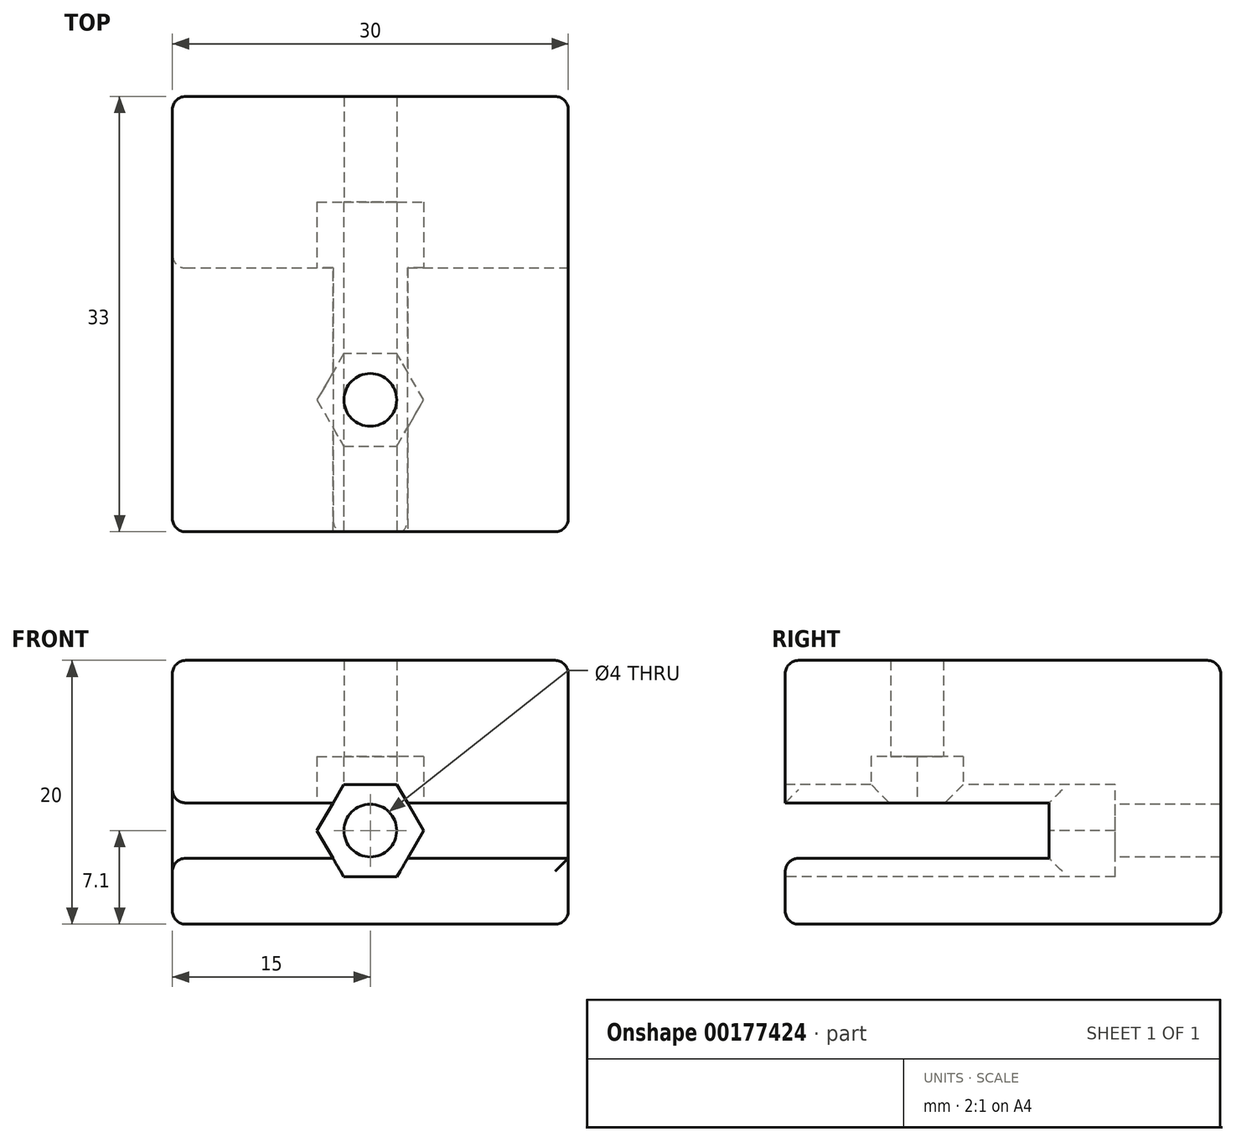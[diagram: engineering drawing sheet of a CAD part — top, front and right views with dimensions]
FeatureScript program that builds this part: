
annotation { "Feature Type Name" : "Feature", "Feature Type Description" : "" }
export const myFeature = defineFeature(function(context is Context, id is Id, definition is map)
    precondition{}
    {
        {
            var Q0;
            Q0=qCreatedBy(makeId("Top.planeOp"),FACE);
            var sketch = newSketch(context, id + "F0", { "sketchPlane" : qUnion([Q0])});
            skLineSegment(sketch, "E0.bottom", {"start": v(-15, 16.5) * mm, "end": v(15, 16.5) * mm});
            skLineSegment(sketch, "E0.top", {"start": v(-15, -16.5) * mm, "end": v(15, -16.5) * mm});
            skLineSegment(sketch, "E0.left", {"start": v(-15, 16.5) * mm, "end": v(-15, -16.5) * mm});
            skLineSegment(sketch, "E0.right", {"start": v(15, 16.5) * mm, "end": v(15, -16.5) * mm});
            skSolve(sketch);
        }
        {
            var Q0;
            Q0=makeQuery(id+"F0.imprint","IMPRINT",FACE,{"disambiguationData":[TD([[makeQuery(id+"F0.imprint","IMPRINT",EDGE,{"derivedFrom":sQuery(id+"F0.wireOp",EDGE,"E0.bottom")}),-1.0]])]});
            extrude(context, id + "F1", {"entities" : qUnion([Q0]), "depth" : 20 * mm});
        }
        {
            var Q0;
            Q0=makeQuery(id+"F1.opExtrude","SWEPT_FACE",FACE,{"disambiguationData":[OSD([sQuery(id+"F0.wireOp",EDGE,"E0.right")])]});
            var sketch = newSketch(context, id + "F2", { "sketchPlane" : qUnion([Q0])});
            skLineSegment(sketch, "E1", {"start": v(-16.5, 5) * mm, "end": v(3.5, 5) * mm});
            skLineSegment(sketch, "E2", {"start": v(3.5, 5) * mm, "end": v(3.5, 9.2) * mm});
            skLineSegment(sketch, "E3", {"start": v(3.5, 9.2) * mm, "end": v(-16.5, 9.2) * mm});
            skSolve(sketch);
        }
        {
            var Q0;
            {var subQ0=sQuery(id+"F2.wireOp",EDGE,"E1");Q0=makeQuery(id+"F2.imprint","IMPRINT",FACE,{"disambiguationData":[TD([[makeQuery(id+"F2.imprint","IMPRINT",EDGE,{"derivedFrom":subQ0}),1.0]])]});}
            extrude(context, id + "F3", {"entities" : qUnion([Q0]), "operationType" : NewBodyOperationType.REMOVE, "endBound" : BoundingType.THROUGH_ALL, "oppositeDirection" : true, "depth" : 25 * mm});
        }
        {
            var Q0;
            Q0=makeQuery(id+"F3.boolean.opBoolean","COPY",FACE,{"derivedFrom":makeQuery(id+"F3.opExtrude","SWEPT_FACE",FACE,{"disambiguationData":[OSD([sQuery(id+"F2.wireOp",EDGE,"E2")])]})});
            var sketch = newSketch(context, id + "F4", { "sketchPlane" : qUnion([Q0])});
            skPoint(sketch, "E4", {"position": v(0, 7.1) * mm});
            skCircle(sketch, "E5.cCircle", {"center": v(0, 7.1) * mm, "radius": 3.5 * mm, "construction": true});
            skLineSegment(sketch, "E5.0", {"start": v(2.02, 3.6) * mm, "end": v(-2.02, 3.6) * mm});
            skLineSegment(sketch, "E5.1", {"start": v(-2.02, 3.6) * mm, "end": v(-4.04, 7.1) * mm});
            skLineSegment(sketch, "E5.2", {"start": v(-4.04, 7.1) * mm, "end": v(-2.02, 10.6) * mm});
            skLineSegment(sketch, "E5.3", {"start": v(-2.02, 10.6) * mm, "end": v(2.02, 10.6) * mm});
            skLineSegment(sketch, "E5.4", {"start": v(2.02, 10.6) * mm, "end": v(4.04, 7.1) * mm});
            skLineSegment(sketch, "E5.5", {"start": v(4.04, 7.1) * mm, "end": v(2.02, 3.6) * mm});
            skPoint(sketch, "E5.0.midPoint", {"position": v(0, 3.6) * mm});
            skCircle(sketch, "E6", {"center": v(0, 7.1) * mm, "radius": 2 * mm});
            skSolve(sketch);
        }
        {
            var Q0;
            {var subQ0=sQuery(id+"F4.wireOp",EDGE,"E5.3");Q0=makeQuery(id+"F4.imprint","IMPRINT",FACE,{"disambiguationData":[TD([[makeQuery(id+"F4.imprint","IMPRINT",EDGE,{"derivedFrom":subQ0}),-1.0]])]});}
            var Q1;
            {var subQ8=sQuery(id+"F4.wireOp",EDGE,"E5.2");var subQ9=sQuery(id+"F4.wireOp",EDGE,"E5.1");var subQ10=makeQuery(id+"F4.imprint","INTERSECT",VERTEX,{"derivedFrom":[subQ9,subQ8]});Q1=makeQuery(id+"F4.imprint","IMPRINT",FACE,{"disambiguationData":[TD([[makeQuery(id+"F4.imprint","IMPRINT",EDGE,{"disambiguationData":[TD([[subQ10,1.0]])],"derivedFrom":subQ9}),-1.0]])]});}
            var Q2;
            {var subQ0=sQuery(id+"F4.wireOp",EDGE,"E5.0");Q2=makeQuery(id+"F4.imprint","IMPRINT",FACE,{"disambiguationData":[TD([[makeQuery(id+"F4.imprint","IMPRINT",EDGE,{"derivedFrom":subQ0}),-1.0]])]});}
            extrude(context, id + "F5", {"entities" : qUnion([Q0, Q1, Q2]), "operationType" : NewBodyOperationType.REMOVE, "oppositeDirection" : true, "depth" : 5 * mm, "hasSecondDirection" : true, "secondDirectionBound" : SecondDirectionBoundingType.THROUGH_ALL, "secondDirectionOppositeDirection" : false, "secondDirectionDepth" : 25 * mm});
        }
        {
            var Q0;
            Q0=makeQuery(id+"F5.boolean.opBoolean","SPLIT",FACE,{"disambiguationData":[TD([makeQuery(id+"F5.opExtrude","SWEPT_FACE",FACE,{"disambiguationData":[OSD([sQuery(id+"F4.wireOp",EDGE,"E6")])]})])],"derivedFrom":makeQuery(id+"F3.boolean.opBoolean","COPY",FACE,{"derivedFrom":makeQuery(id+"F3.opExtrude","SWEPT_FACE",FACE,{"disambiguationData":[OSD([sQuery(id+"F2.wireOp",EDGE,"E2")])]})})});
            extrude(context, id + "F6", {"entities" : qUnion([Q0]), "operationType" : NewBodyOperationType.REMOVE, "endBound" : BoundingType.THROUGH_ALL, "oppositeDirection" : true, "depth" : 25 * mm});
        }
        {
            var Q0;
            Q0=makeQuery(id+"F5.boolean.opBoolean","SPLIT",FACE,{"disambiguationData":[TD([makeQuery(id+"F1.opExtrude","SWEPT_FACE",FACE,{"disambiguationData":[OSD([sQuery(id+"F0.wireOp",EDGE,"E0.left")])]})])],"derivedFrom":makeQuery(id+"F3.boolean.opBoolean","COPY",FACE,{"derivedFrom":makeQuery(id+"F3.opExtrude","SWEPT_FACE",FACE,{"disambiguationData":[OSD([sQuery(id+"F2.wireOp",EDGE,"E3")])]})})});
            var sketch = newSketch(context, id + "F7", { "sketchPlane" : qUnion([Q0])});
            skPoint(sketch, "E7", {"position": v(0, 6.5) * mm});
            skLineSegment(sketch, "E8.0.0", {"start": v(-2.83, -3.5) * mm, "end": v(-2.83, 16.5) * mm});
            skLineSegment(sketch, "E8.0.1", {"start": v(-2.83, 16.5) * mm, "end": v(-15, 16.5) * mm});
            skLineSegment(sketch, "E8.0.2", {"start": v(-15, 16.5) * mm, "end": v(-15, -3.5) * mm});
            skLineSegment(sketch, "E8.0.3", {"start": v(-15, -3.5) * mm, "end": v(-2.83, -3.5) * mm});
            skLineSegment(sketch, "E9.0.0", {"start": v(2.83, 16.5) * mm, "end": v(2.83, -3.5) * mm});
            skLineSegment(sketch, "E9.0.1", {"start": v(2.83, -3.5) * mm, "end": v(15, -3.5) * mm});
            skLineSegment(sketch, "E9.0.2", {"start": v(15, -3.5) * mm, "end": v(15, 16.5) * mm});
            skLineSegment(sketch, "E9.0.3", {"start": v(15, 16.5) * mm, "end": v(2.83, 16.5) * mm});
            skCircle(sketch, "E10", {"center": v(0, 6.5) * mm, "radius": 2 * mm});
            skCircle(sketch, "E11.cCircle", {"center": v(0, 6.5) * mm, "radius": 3.5 * mm, "construction": true});
            skLineSegment(sketch, "E11.0", {"start": v(2.02, 3) * mm, "end": v(-2.02, 3) * mm});
            skLineSegment(sketch, "E11.1", {"start": v(-2.02, 3) * mm, "end": v(-4.04, 6.5) * mm});
            skLineSegment(sketch, "E11.2", {"start": v(-4.04, 6.5) * mm, "end": v(-2.02, 10) * mm});
            skLineSegment(sketch, "E11.3", {"start": v(-2.02, 10) * mm, "end": v(2.02, 10) * mm});
            skLineSegment(sketch, "E11.4", {"start": v(2.02, 10) * mm, "end": v(4.04, 6.5) * mm});
            skLineSegment(sketch, "E11.5", {"start": v(4.04, 6.5) * mm, "end": v(2.02, 3) * mm});
            skPoint(sketch, "E11.0.midPoint", {"position": v(0, 3) * mm});
            skSolve(sketch);
        }
        {
            var Q0;
            Q0=makeQuery(id+"F7.imprint","IMPRINT",FACE,{"disambiguationData":[TD([[makeQuery(id+"F7.imprint","IMPRINT",EDGE,{"derivedFrom":sQuery(id+"F7.wireOp",EDGE,"E10")}),1.0]])]});
            extrude(context, id + "F8", {"entities" : qUnion([Q0]), "operationType" : NewBodyOperationType.REMOVE, "endBound" : BoundingType.THROUGH_ALL, "oppositeDirection" : true, "depth" : 25 * mm});
        }
        {
            var Q0;
            Q0=makeQuery(id+"F7.imprint","IMPRINT",FACE,{"disambiguationData":[TD([[makeQuery(id+"F7.imprint","IMPRINT",EDGE,{"derivedFrom":sQuery(id+"F7.wireOp",EDGE,"E10")}),-1.0]])]});
            var Q1;
            {var subQ0=sQuery(id+"F7.wireOp",EDGE,"E11.2");var subQ1=sQuery(id+"F7.wireOp",EDGE,"E8.0.0");var subQ2=makeQuery(id+"F7.imprint","INTERSECT",VERTEX,{"derivedFrom":[subQ1,subQ0]});Q1=makeQuery(id+"F7.imprint","IMPRINT",FACE,{"disambiguationData":[TD([[makeQuery(id+"F7.imprint","IMPRINT",EDGE,{"disambiguationData":[TD([[subQ2,-1.0]])],"derivedFrom":subQ1}),-1.0]])]});}
            var Q2;
            {var subQ0=sQuery(id+"F7.wireOp",EDGE,"E11.4");var subQ1=sQuery(id+"F7.wireOp",EDGE,"E9.0.0");var subQ2=makeQuery(id+"F7.imprint","INTERSECT",VERTEX,{"derivedFrom":[subQ1,subQ0]});Q2=makeQuery(id+"F7.imprint","IMPRINT",FACE,{"disambiguationData":[TD([[makeQuery(id+"F7.imprint","IMPRINT",EDGE,{"disambiguationData":[TD([[subQ2,-1.0]])],"derivedFrom":subQ1}),1.0]])]});}
            extrude(context, id + "F9", {"entities" : qUnion([Q0, Q1, Q2]), "operationType" : NewBodyOperationType.REMOVE, "oppositeDirection" : true, "depth" : 3.5 * mm});
        }
        {
            var Q0;
            Q0=makeQuery(id+"F1.opExtrude","CAP_EDGE",EDGE,{"disambiguationData":[OSD([sQuery(id+"F0.wireOp",EDGE,"E0.bottom")])],"isStart":true});
            var Q1;
            Q1=makeQuery(id+"F1.opExtrude","SWEPT_EDGE",EDGE,{"disambiguationData":[OSD([sQuery(id+"F0.wireOp",EDGE,"E0.bottom"),sQuery(id+"F0.wireOp",EDGE,"E0.right")])]});
            var Q2;
            Q2=makeQuery(id+"F1.opExtrude","CAP_EDGE",EDGE,{"disambiguationData":[OSD([sQuery(id+"F0.wireOp",EDGE,"E0.bottom")])],"isStart":false});
            var Q3;
            Q3=makeQuery(id+"F1.opExtrude","SWEPT_EDGE",EDGE,{"disambiguationData":[OSD([sQuery(id+"F0.wireOp",EDGE,"E0.bottom"),sQuery(id+"F0.wireOp",EDGE,"E0.left")])]});
            var Q4;
            Q4=makeQuery(id+"F1.opExtrude","CAP_EDGE",EDGE,{"disambiguationData":[OSD([sQuery(id+"F0.wireOp",EDGE,"E0.left")])],"isStart":true});
            var Q5;
            Q5=makeQuery(id+"F1.opExtrude","CAP_EDGE",EDGE,{"disambiguationData":[OSD([sQuery(id+"F0.wireOp",EDGE,"E0.top")])],"isStart":true});
            var Q6;
            Q6=makeQuery(id+"F1.opExtrude","CAP_EDGE",EDGE,{"disambiguationData":[OSD([sQuery(id+"F0.wireOp",EDGE,"E0.right")])],"isStart":true});
            var Q7;
            Q7=makeQuery(id+"F1.opExtrude","CAP_EDGE",EDGE,{"disambiguationData":[OSD([sQuery(id+"F0.wireOp",EDGE,"E0.left")])],"isStart":false});
            var Q8;
            Q8=makeQuery(id+"F1.opExtrude","CAP_EDGE",EDGE,{"disambiguationData":[OSD([sQuery(id+"F0.wireOp",EDGE,"E0.top")])],"isStart":false});
            var Q9;
            Q9=makeQuery(id+"F1.opExtrude","CAP_EDGE",EDGE,{"disambiguationData":[OSD([sQuery(id+"F0.wireOp",EDGE,"E0.right")])],"isStart":false});
            var Q10;
            {var subQ0=sQuery(id+"F0.wireOp",EDGE,"E0.left");var subQ1=sQuery(id+"F0.wireOp",EDGE,"E0.top");Q10=makeQuery(id+"F3.boolean.opBoolean","SPLIT",EDGE,{"disambiguationData":[TD([makeQuery(id+"F3.opExtrude","SWEPT_FACE",FACE,{"disambiguationData":[OSD([sQuery(id+"F2.wireOp",EDGE,"E1")])]})])],"derivedFrom":makeQuery(id+"F1.opExtrude","SWEPT_EDGE",EDGE,{"disambiguationData":[OSD([subQ1,subQ0])]})});}
            var Q11;
            {var subQ0=sQuery(id+"F0.wireOp",EDGE,"E0.left");var subQ1=sQuery(id+"F0.wireOp",EDGE,"E0.top");Q11=makeQuery(id+"F3.boolean.opBoolean","SPLIT",EDGE,{"disambiguationData":[TD([makeQuery(id+"F3.opExtrude","SWEPT_FACE",FACE,{"disambiguationData":[OSD([sQuery(id+"F2.wireOp",EDGE,"E3")])]})])],"derivedFrom":makeQuery(id+"F1.opExtrude","SWEPT_EDGE",EDGE,{"disambiguationData":[OSD([subQ1,subQ0])]})});}
            var Q12;
            {var subQ0=sQuery(id+"F0.wireOp",EDGE,"E0.right");var subQ1=sQuery(id+"F0.wireOp",EDGE,"E0.top");Q12=makeQuery(id+"F3.boolean.opBoolean","SPLIT",EDGE,{"disambiguationData":[TD([makeQuery(id+"F3.opExtrude","SWEPT_FACE",FACE,{"disambiguationData":[OSD([sQuery(id+"F2.wireOp",EDGE,"E1")])]})])],"derivedFrom":makeQuery(id+"F1.opExtrude","SWEPT_EDGE",EDGE,{"disambiguationData":[OSD([subQ1,subQ0])]})});}
            var Q13;
            {var subQ0=sQuery(id+"F0.wireOp",EDGE,"E0.right");var subQ1=sQuery(id+"F0.wireOp",EDGE,"E0.top");Q13=makeQuery(id+"F3.boolean.opBoolean","SPLIT",EDGE,{"disambiguationData":[TD([makeQuery(id+"F3.opExtrude","SWEPT_FACE",FACE,{"disambiguationData":[OSD([sQuery(id+"F2.wireOp",EDGE,"E3")])]})])],"derivedFrom":makeQuery(id+"F1.opExtrude","SWEPT_EDGE",EDGE,{"disambiguationData":[OSD([subQ1,subQ0])]})});}
            var Q14;
            Q14=makeQuery(id+"F3.boolean.opBoolean","COPY",EDGE,{"derivedFrom":makeQuery(id+"F3.opExtrude","CAP_EDGE",EDGE,{"disambiguationData":[OSD([sQuery(id+"F2.wireOp",EDGE,"E3")])],"isStart":true})});
            var Q15;
            Q15=makeQuery(id+"F3.boolean.opBoolean","COPY",EDGE,{"derivedFrom":makeQuery(id+"F3.opExtrude","CAP_EDGE",EDGE,{"disambiguationData":[OSD([sQuery(id+"F2.wireOp",EDGE,"E1")])],"isStart":true})});
            var Q16;
            {var subQ0=sQuery(id+"F0.wireOp",EDGE,"E0.top");var subQ1=sQuery(id+"F0.wireOp",EDGE,"E0.right");var subQ2=sQuery(id+"F2.wireOp",EDGE,"E1");Q16=makeQuery(id+"F5.boolean.opBoolean","SPLIT",EDGE,{"disambiguationData":[TD([makeQuery(id+"F1.opExtrude","SWEPT_FACE",FACE,{"disambiguationData":[OSD([subQ1])]})])],"derivedFrom":makeQuery(id+"F3.boolean.opBoolean","COPY",EDGE,{"derivedFrom":makeQuery(id+"F3.opExtrude","SWEPT_EDGE",EDGE,{"disambiguationData":[OSD([subQ0,subQ1,subQ2])]})})});}
            var Q17;
            {var subQ0=sQuery(id+"F0.wireOp",EDGE,"E0.top");var subQ1=sQuery(id+"F2.wireOp",EDGE,"E1");Q17=makeQuery(id+"F5.boolean.opBoolean","SPLIT",EDGE,{"disambiguationData":[TD([makeQuery(id+"F1.opExtrude","SWEPT_FACE",FACE,{"disambiguationData":[OSD([sQuery(id+"F0.wireOp",EDGE,"E0.left")])]})])],"derivedFrom":makeQuery(id+"F3.boolean.opBoolean","COPY",EDGE,{"derivedFrom":makeQuery(id+"F3.opExtrude","SWEPT_EDGE",EDGE,{"disambiguationData":[OSD([subQ0,sQuery(id+"F0.wireOp",EDGE,"E0.right"),subQ1])]})})});}
            var Q18;
            {var subQ0=sQuery(id+"F0.wireOp",EDGE,"E0.top");var subQ1=sQuery(id+"F2.wireOp",EDGE,"E3");Q18=makeQuery(id+"F5.boolean.opBoolean","SPLIT",EDGE,{"disambiguationData":[TD([makeQuery(id+"F1.opExtrude","SWEPT_FACE",FACE,{"disambiguationData":[OSD([sQuery(id+"F0.wireOp",EDGE,"E0.left")])]})])],"derivedFrom":makeQuery(id+"F3.boolean.opBoolean","COPY",EDGE,{"derivedFrom":makeQuery(id+"F3.opExtrude","SWEPT_EDGE",EDGE,{"disambiguationData":[OSD([subQ0,sQuery(id+"F0.wireOp",EDGE,"E0.right"),subQ1])]})})});}
            var Q19;
            Q19=makeQuery(id+"F3.boolean.opBoolean","INTERSECT",EDGE,{"derivedFrom":[makeQuery(id+"F1.opExtrude","SWEPT_FACE",FACE,{"disambiguationData":[OSD([sQuery(id+"F0.wireOp",EDGE,"E0.left")])]}),makeQuery(id+"F3.opExtrude","SWEPT_FACE",FACE,{"disambiguationData":[OSD([sQuery(id+"F2.wireOp",EDGE,"E2")])]})]});
            var Q20;
            Q20=makeQuery(id+"F3.boolean.opBoolean","INTERSECT",EDGE,{"derivedFrom":[makeQuery(id+"F1.opExtrude","SWEPT_FACE",FACE,{"disambiguationData":[OSD([sQuery(id+"F0.wireOp",EDGE,"E0.left")])]}),makeQuery(id+"F3.opExtrude","SWEPT_FACE",FACE,{"disambiguationData":[OSD([sQuery(id+"F2.wireOp",EDGE,"E1")])]})]});
            var Q21;
            Q21=makeQuery(id+"F3.boolean.opBoolean","INTERSECT",EDGE,{"derivedFrom":[makeQuery(id+"F1.opExtrude","SWEPT_FACE",FACE,{"disambiguationData":[OSD([sQuery(id+"F0.wireOp",EDGE,"E0.left")])]}),makeQuery(id+"F3.opExtrude","SWEPT_FACE",FACE,{"disambiguationData":[OSD([sQuery(id+"F2.wireOp",EDGE,"E3")])]})]});
            var Q22;
            Q22=makeQuery(id+"F3.boolean.opBoolean","COPY",EDGE,{"derivedFrom":makeQuery(id+"F3.opExtrude","CAP_EDGE",EDGE,{"disambiguationData":[OSD([sQuery(id+"F2.wireOp",EDGE,"E2")])],"isStart":true})});
            fillet(context, id + "F10", {"entities" : qUnion([Q0, Q1, Q2, Q3, Q4, Q5, Q6, Q7, Q8, Q9, Q10, Q11, Q12, Q13, Q14, Q15, Q16, Q17, Q18, Q19, Q20, Q21, Q22]), "radius" : 1 * mm, "tangentPropagation" : true, "allowEdgeOverflow" : false});
        }
    });
